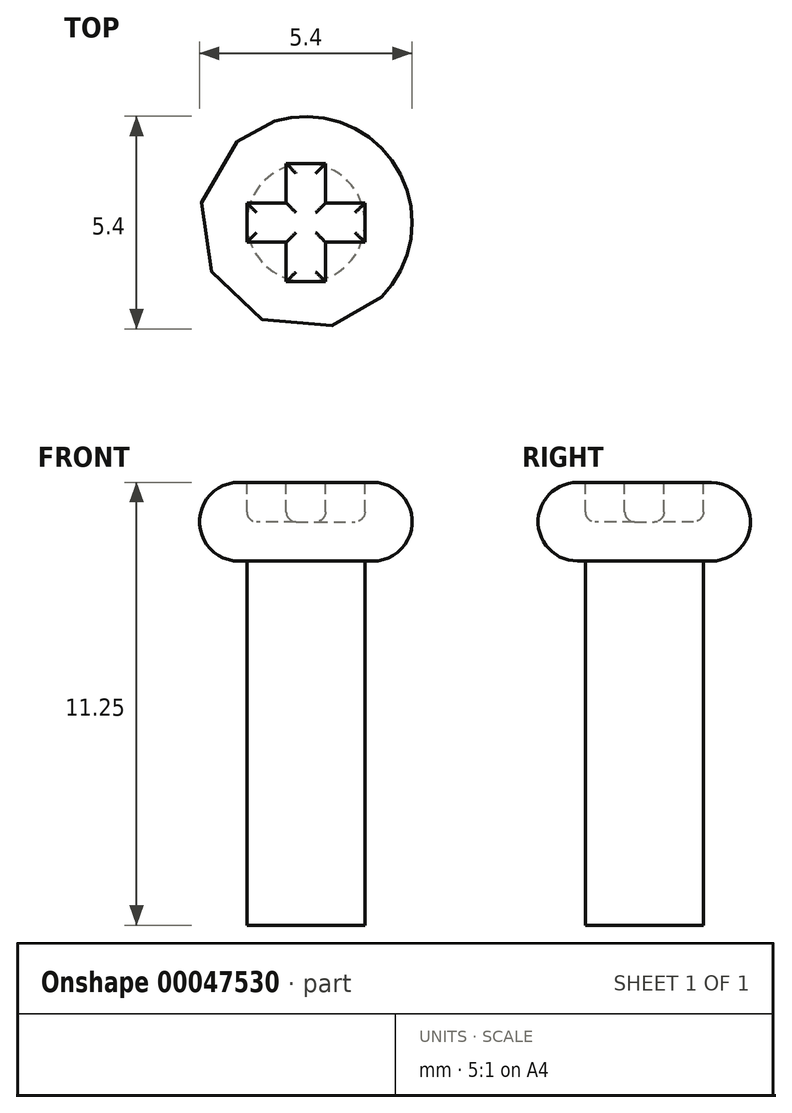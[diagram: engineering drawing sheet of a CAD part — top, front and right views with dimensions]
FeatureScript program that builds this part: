
annotation { "Feature Type Name" : "Feature", "Feature Type Description" : "" }
export const myFeature = defineFeature(function(context is Context, id is Id, definition is map)
    precondition{}
    {
        {
            var Q0;
            Q0=qCreatedBy(makeId("Top.planeOp"),FACE);
            var sketch = newSketch(context, id + "F0", { "sketchPlane" : qUnion([Q0])});
            skCircle(sketch, "E0", {"center": v(0, 0) * mm, "radius": 1.5 * mm});
            skSolve(sketch);
        }
        {
            var Q0;
            Q0 = qSketchRegion(id + "F0", true);
            extrude(context, id + "F1", {"entities" : qUnion([Q0]), "depth" : 9.25 * mm});
        }
        {
            var Q0;
            Q0=makeQuery(id+"F1.opExtrude","CAP_FACE",FACE,{"disambiguationData":[OSD([sQuery(id+"F0.wireOp",EDGE,"E0")])],"isStart":false});
            var sketch = newSketch(context, id + "F2", { "sketchPlane" : qUnion([Q0])});
            skCircle(sketch, "E1", {"center": v(0, 0) * mm, "radius": 2.7 * mm});
            skSolve(sketch);
        }
        {
            var Q0;
            Q0 = qSketchRegion(id + "F2", true);
            extrude(context, id + "F3", {"entities" : qUnion([Q0]), "operationType" : NewBodyOperationType.ADD, "depth" : 2 * mm});
        }
        {
            var Q0;
            Q0=makeQuery(id+"F3.opExtrude","CAP_FACE",FACE,{"disambiguationData":[OSD([sQuery(id+"F2.wireOp",EDGE,"E1")])],"isStart":false});
            var sketch = newSketch(context, id + "F4", { "sketchPlane" : qUnion([Q0])});
            skLineSegment(sketch, "E2", {"start": v(-0.5, 1.5) * mm, "end": v(0.5, 1.5) * mm});
            skLineSegment(sketch, "E3", {"start": v(-0.5, -1.5) * mm, "end": v(0.5, -1.5) * mm});
            skLineSegment(sketch, "E4", {"start": v(-0.5, 1.5) * mm, "end": v(-0.5, 0.5) * mm});
            skLineSegment(sketch, "E5", {"start": v(0.5, 1.5) * mm, "end": v(0.5, 0.5) * mm});
            skLineSegment(sketch, "E6", {"start": v(-1.5, -0.5) * mm, "end": v(-0.5, -0.5) * mm});
            skLineSegment(sketch, "E7", {"start": v(1.5, -0.5) * mm, "end": v(1.5, 0.5) * mm});
            skLineSegment(sketch, "E8", {"start": v(1.5, 0.5) * mm, "end": v(0.5, 0.5) * mm});
            skLineSegment(sketch, "E9", {"start": v(-1.5, 0.5) * mm, "end": v(-1.5, -0.5) * mm});
            skLineSegment(sketch, "E10.trimOffspring", {"start": v(-0.5, -0.5) * mm, "end": v(-0.5, -1.5) * mm});
            skLineSegment(sketch, "E11.trimOffspring", {"start": v(-0.5, 0.5) * mm, "end": v(-1.5, 0.5) * mm});
            skLineSegment(sketch, "E12.trimOffspring", {"start": v(0.5, -0.5) * mm, "end": v(0.5, -1.5) * mm});
            skLineSegment(sketch, "E13.trimOffspring", {"start": v(0.5, -0.5) * mm, "end": v(1.5, -0.5) * mm});
            skSolve(sketch);
        }
        {
            var Q0;
            Q0 = qSketchRegion(id + "F4", true);
            extrude(context, id + "F5", {"entities" : qUnion([Q0]), "operationType" : NewBodyOperationType.REMOVE, "oppositeDirection" : true, "depth" : 1 * mm});
        }
        {
            var Q0;
            Q0=makeQuery(id+"F5.boolean.opBoolean","COPY",FACE,{"derivedFrom":makeQuery(id+"F5.opExtrude","CAP_FACE",FACE,{"disambiguationData":[OSD([sQuery(id+"F4.wireOp",EDGE,"E2"),sQuery(id+"F4.wireOp",EDGE,"E3"),sQuery(id+"F4.wireOp",EDGE,"E4"),sQuery(id+"F4.wireOp",EDGE,"E5"),sQuery(id+"F4.wireOp",EDGE,"E6"),sQuery(id+"F4.wireOp",EDGE,"E7"),sQuery(id+"F4.wireOp",EDGE,"E8"),sQuery(id+"F4.wireOp",EDGE,"E9"),sQuery(id+"F4.wireOp",EDGE,"E10.trimOffspring"),sQuery(id+"F4.wireOp",EDGE,"E11.trimOffspring"),sQuery(id+"F4.wireOp",EDGE,"E12.trimOffspring"),sQuery(id+"F4.wireOp",EDGE,"E13.trimOffspring")])],"isStart":false})});
            fillet(context, id + "F6", {"entities" : qUnion([Q0]), "radius" : .25 * mm, "tangentPropagation" : true, "allowEdgeOverflow" : false});
        }
        {
            var Q0;
            Q0=makeQuery(id+"F3.opExtrude","SWEPT_FACE",FACE,{"disambiguationData":[OSD([sQuery(id+"F2.wireOp",EDGE,"E1")])]});
            fillet(context, id + "F7", {"entities" : qUnion([Q0]), "radius" : 1 * mm, "tangentPropagation" : true, "allowEdgeOverflow" : false});
        }
    });
